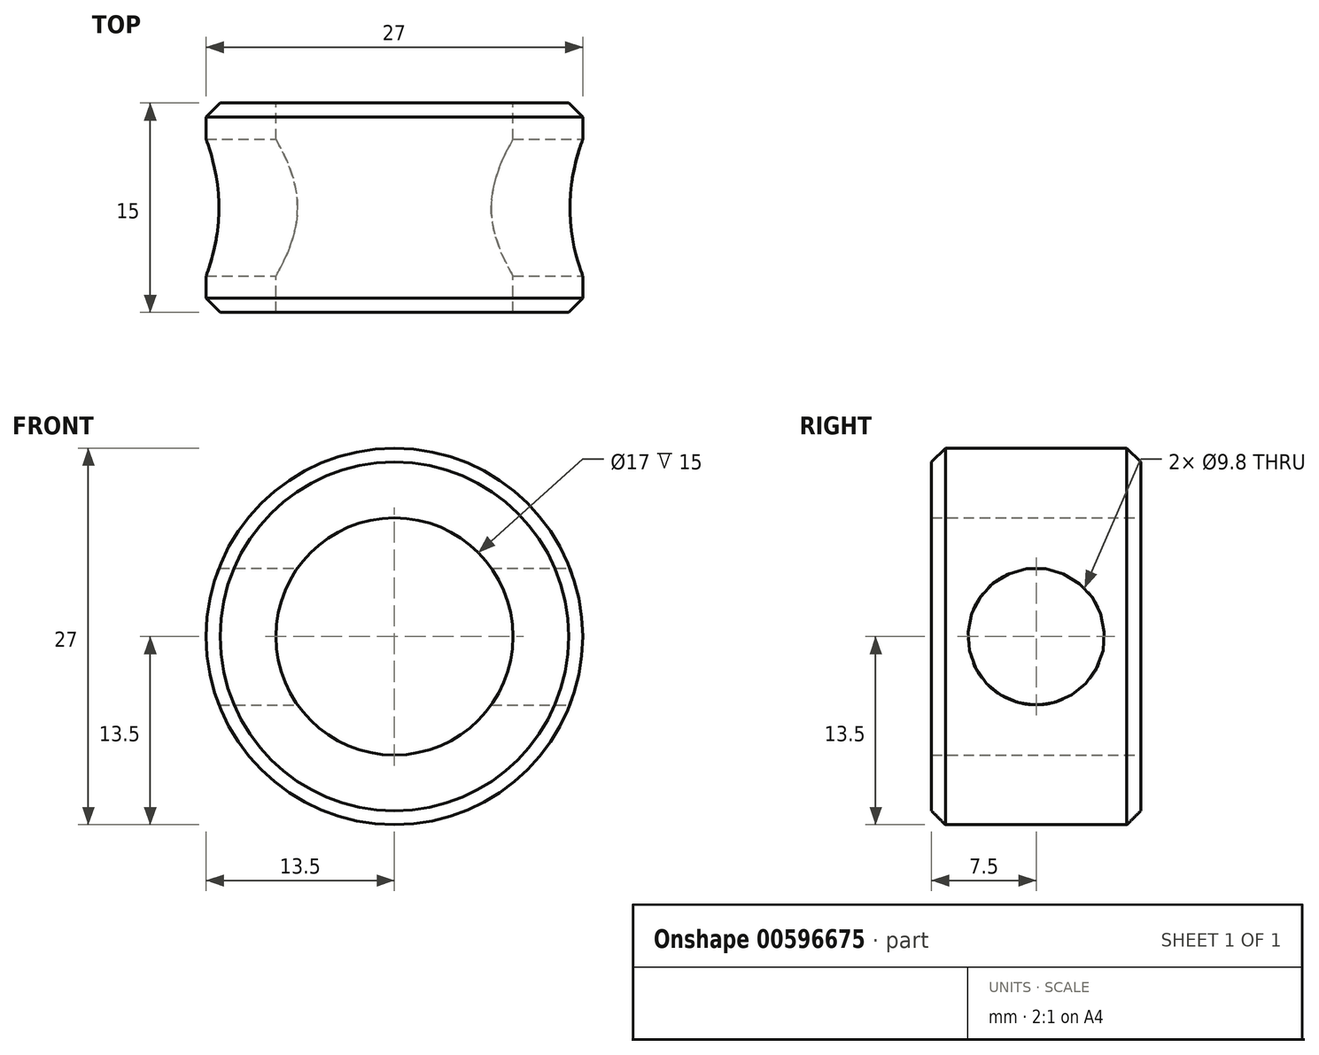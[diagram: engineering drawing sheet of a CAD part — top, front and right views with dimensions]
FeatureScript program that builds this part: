
annotation { "Feature Type Name" : "Feature", "Feature Type Description" : "" }
export const myFeature = defineFeature(function(context is Context, id is Id, definition is map)
    precondition{}
    {
        {
            var Q0;
            Q0=qCreatedBy(makeId("Front.planeOp"),FACE);
            var sketch = newSketch(context, id + "F0", { "sketchPlane" : qUnion([Q0])});
            skCircle(sketch, "E0", {"center": v(0, 0) * mm, "radius": 13.5 * mm});
            skCircle(sketch, "E1", {"center": v(0, 0) * mm, "radius": 8.5 * mm});
            skSolve(sketch);
        }
        {
            var Q0;
            Q0 = qSketchRegion(id + "F0", true);
            extrude(context, id + "F1", {"entities" : qUnion([Q0]), "depth" : 15 * mm, "offsetDistance" : 25 * mm, "symmetric" : true});
        }
        {
            var Q0;
            Q0=qCreatedBy(makeId("Right.planeOp"),FACE);
            var sketch = newSketch(context, id + "F2", { "sketchPlane" : qUnion([Q0])});
            skCircle(sketch, "E2", {"center": v(0, 0) * mm, "radius": 4.9 * mm});
            skSolve(sketch);
        }
        {
            var Q0;
            Q0 = qSketchRegion(id + "F2", true);
            extrude(context, id + "F3", {"entities" : qUnion([Q0]), "operationType" : NewBodyOperationType.REMOVE, "oppositeDirection" : true, "depth" : 30 * mm, "offsetDistance" : 25 * mm, "symmetric" : true});
        }
        {
            var Q0;
            Q0=makeQuery(id+"F1.opExtrude","CAP_EDGE",EDGE,{"disambiguationData":[OSD([sQuery(id+"F0.wireOp",EDGE,"E0")])],"isStart":false});
            var Q1;
            Q1=makeQuery(id+"F1.opExtrude","CAP_EDGE",EDGE,{"disambiguationData":[OSD([sQuery(id+"F0.wireOp",EDGE,"E0")])],"isStart":true});
            chamfer(context, id + "F4", {"entities" : qUnion([Q0, Q1]), "width" : 1 * mm, "tangentPropagation" : true});
        }
    });
